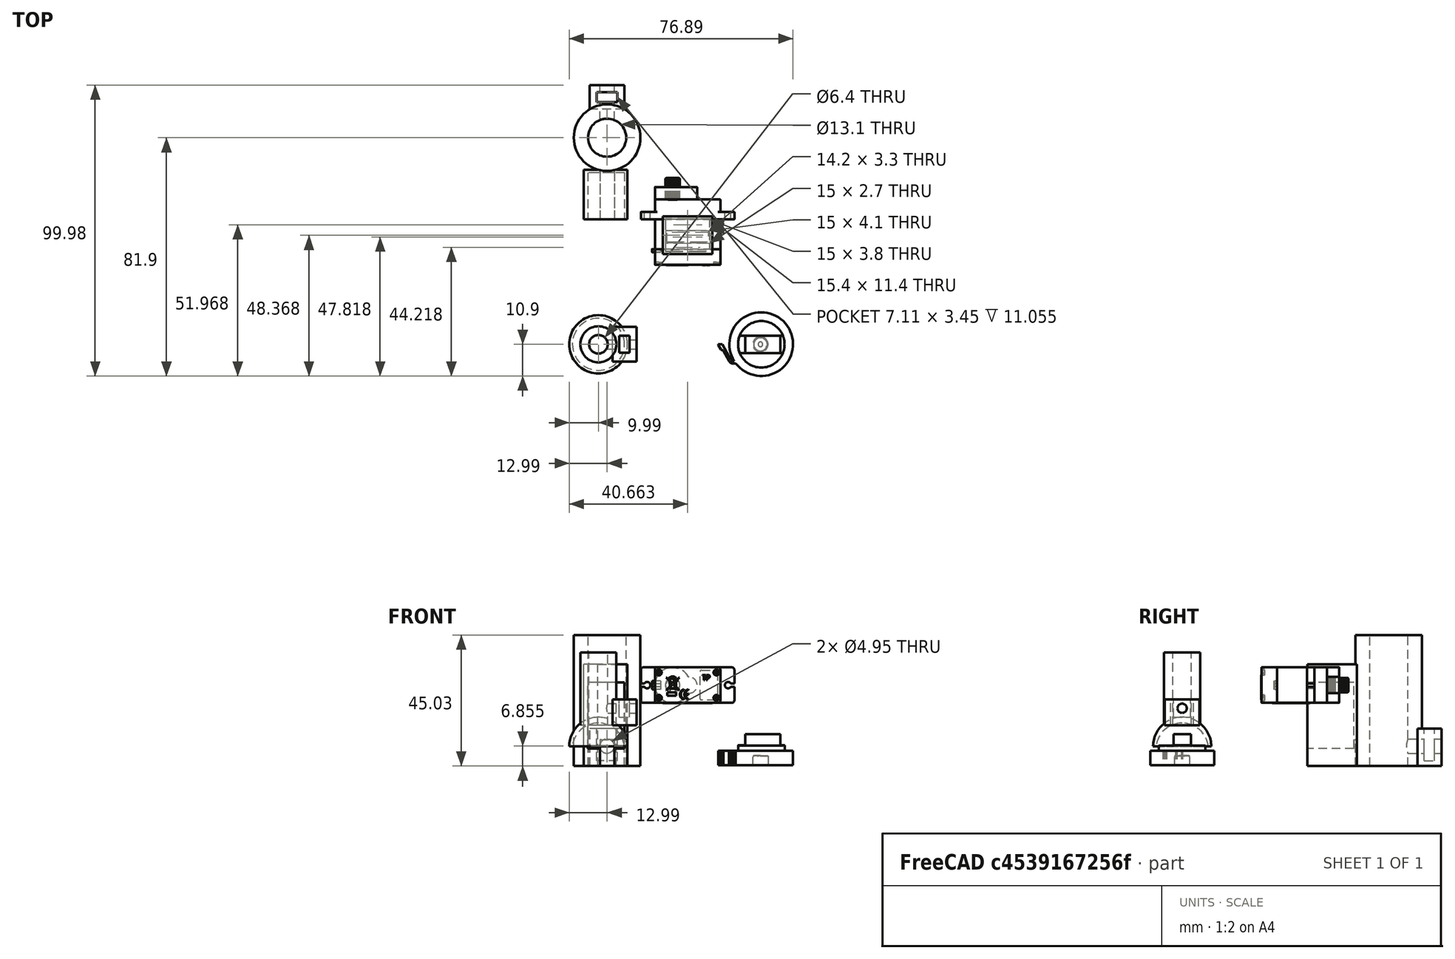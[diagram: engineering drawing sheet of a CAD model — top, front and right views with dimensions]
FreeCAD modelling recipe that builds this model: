
FCSTD DOCUMENT  (FreeCAD 0.19R24366 (Git))
Label: motor_fit_servo
License: All rights reserved
LicenseURL: http://en.wikipedia.org/wiki/All_rights_reserved
objects: Part::Feature×15, Part::Box×11, Part::Cut×9, Part::Cylinder×7, Part::Fuse×4, Part::MultiFuse×4, Sketcher::SketchObject×3, Mesh::Feature×2, Part::Extrusion×2, Part::Sphere×2, Part::Compound×2, Part::Compound2×1
note: 59 computed .brp shape members not serialized (recipe doc carries the construction recipe); baked Part::Feature solids carry a one-line shape summary decoded from their .brp

FEATURE [Part::Cylinder] cylinder
  Angle = 360
  AttacherType = Attacher::AttachEngine3D
  Height = 45
  Radius = 11.45
FEATURE [Part::Box] cube
  AttacherType = Attacher::AttachEngine3D
  Height = 12.91
  Length = 8.25
  Placement = pos=(-4.125,-5.955,-6.455) rot=(0,0,1;0rad)
  Width = 11.91
FEATURE [Part::Box] cube001
  AttacherType = Attacher::AttachEngine3D
  Height = 11.11
  Length = 3.45
  Placement = pos=(-1.725,-3.555,-4.6) rot=(0,0,1;0rad)
  Width = 7.11
FEATURE [Part::Cut] difference
  Base = -> cube
  Placement = pos=(13.95,0,6.425) rot=(0,0,1;0rad)
  Tool = -> cube001
FEATURE [Part::Fuse] union
  Base = -> cylinder
  Tool = -> difference
FEATURE [Part::Cylinder] cylinder001
  Angle = 360
  AttacherType = Attacher::AttachEngine3D
  Height = 50
  Placement = pos=(0,0,-1) rot=(0,0,1;0rad)
  Radius = 6.55
FEATURE [Part::Cylinder] cylinder002
  Angle = 360
  AttacherType = Attacher::AttachEngine3D
  Height = 22.9
  Placement = pos=(0,0,6.825) rot=(0,1,0;1.5708rad)
  Radius = 2.475
FEATURE [Part::Fuse] union001
  Base = -> cylinder001
  Tool = -> cylinder002
FEATURE [Part::Cut] difference001  label="poleFit"
  Base = -> union
  Tool = -> union001
FEATURE [Part::Box] Box  label="Cube"
  AttacherType = Attacher::AttachEngine3D
  Height = 17
  Length = 22.7
  Placement = pos=(0,0,1) rot=(0,0,1;0rad)
  Width = 12.6
FEATURE [Part::Box] Box001  label="Cube001"
  AttacherType = Attacher::AttachEngine3D
  Height = 17
  Length = 35
  Placement = pos=(-6,-1,0) rot=(0,0,1;0rad)
  Width = 15
FEATURE [Part::Cut] Cut
  Base = -> Box001
  Placement = pos=(-11,-6,6) rot=(0,-1,0;1.5708rad)
  Tool = -> Box
FEATURE [Part::Box] Box002  label="Cube002"
  AttacherType = Attacher::AttachEngine3D
  Height = 10
  Length = 20
  Placement = pos=(-30,-2.5,-1) rot=(0,0,1;0rad)
  Width = 5
FEATURE [Part::Cut] Cut001
  Base = -> Cut
  Tool = -> Box002
FEATURE [Part::MultiFuse] Fusion  label="motor_holder"
  Placement = pos=(-21,50,0) rot=(0,0,1;1.5708rad)
  Shapes = -> [difference001,Cut001]
FEATURE [Part::Feature] Solid
  shape: bbox 22.5 x 10.3 x 12.2 mm, 10 faces (baked)
FEATURE [Part::Feature] Solid001
  shape: bbox 17 x 13 x 0.1 mm, 50 faces (baked)
FEATURE [Part::Feature] Solid002
  shape: bbox 17 x 13 x 0.1 mm, 50 faces (baked)
FEATURE [Part::Feature] Solid003 .. Solid006  x4 (patterned run collapsed; names and placements below)
  shape: bbox 1.933 x 1 x 1.949 mm, 19 faces (baked)
FEATURE [Part::Feature] Solid007
  shape: bbox 22.64 x 5.5 x 12.34 mm, 157 faces (baked)
FEATURE [Part::Feature] Solid008
  shape: bbox 3 x 1 x 1 mm, 4 faces (baked)
FEATURE [Part::Feature] Solid009
  shape: bbox 3 x 1 x 1 mm, 4 faces (baked)
FEATURE [Part::Feature] Solid010
  shape: bbox 3 x 1 x 1 mm, 4 faces (baked)
FEATURE [Part::Feature] Solid011
  shape: bbox 32.1 x 11.05 x 13.21 mm, 102 faces (baked)
FEATURE [Part::Feature] Solid012
  shape: bbox 4.9 x 7.35 x 4.9 mm, 186 faces (baked)
FEATURE [Part::Compound2] Compound  label="SG90 Servo"
  Links = -> [Solid,Solid001,Solid002,Solid003,Solid004,Solid005,Solid006,Solid007,Solid008,Solid009,Solid010,Solid011,Solid012]
  Placement = pos=(-14.6069,45.1539,-46.0545) rot=(1,0,0;1.5708rad)
FEATURE [Mesh::Feature] Base
  Placement = pos=(0,0,0) rot=(1,0,0;1.5708rad)
FEATURE [Mesh::Feature] Freewheel_0_8mm  label="Freewheel_0.8mm"
  Placement = pos=(-63.4529,-2.9298,-37.056) rot=(0,0,1;0rad)
FEATURE [Sketcher::SketchObject] Sketch
  FullyConstrained = true
  Placement = pos=(0,0,0) rot=(0.57735,0.57735,0.57735;2.0944rad)
  sketch-geometry (37):
    g0: LineSegment StartX=76.2334 StartY=-16.1683 StartZ=0 EndX=76.2157 EndY=-16.287 EndZ=0
    g1: LineSegment StartX=76.2157 StartY=-16.287 StartZ=0 EndX=76.2042 EndY=-16.4372 EndZ=0
    g2: LineSegment StartX=76.2042 StartY=-16.4372 StartZ=0 EndX=76.2156 EndY=-16.5892 EndZ=0
    g3: LineSegment StartX=76.2156 StartY=-16.5892 StartZ=0 EndX=76.2528 EndY=-16.7393 EndZ=0
    g4: LineSegment StartX=76.2528 StartY=-16.7393 StartZ=0 EndX=76.312 EndY=-16.8829 EndZ=0
    g5: LineSegment StartX=76.312 StartY=-16.8829 StartZ=0 EndX=76.389 EndY=-17.0118 EndZ=0
    g6: LineSegment StartX=76.389 StartY=-17.0118 StartZ=0 EndX=76.4857 EndY=-17.1291 EndZ=0
    g7: LineSegment StartX=76.4857 StartY=-17.1291 StartZ=0 EndX=76.5997 EndY=-17.2306 EndZ=0
    g8: LineSegment StartX=76.5997 StartY=-17.2306 StartZ=0 EndX=76.7284 EndY=-17.3138 EndZ=0
    g9: LineSegment StartX=76.7284 StartY=-17.3138 StartZ=0 EndX=82.1149 EndY=-20.2387 EndZ=0
    g10: LineSegment StartX=82.1149 StartY=-20.2387 StartZ=0 EndX=82.1149 EndY=-21.7329 EndZ=0
    g11: LineSegment StartX=82.1149 StartY=-21.7329 StartZ=0 EndX=81.7891 EndY=-21.7293 EndZ=0
    g12: LineSegment StartX=81.7891 StartY=-21.7293 StartZ=0 EndX=80.304 EndY=-20.8014 EndZ=0
    g13: LineSegment StartX=80.304 StartY=-20.8014 StartZ=0 EndX=80.2423 EndY=-20.7557 EndZ=0
    g14: LineSegment StartX=80.2423 StartY=-20.7557 StartZ=0 EndX=80.188 EndY=-20.7011 EndZ=0
    g15: LineSegment StartX=80.188 StartY=-20.7011 StartZ=0 EndX=80.1429 EndY=-20.6389 EndZ=0
    g16: LineSegment StartX=80.1429 StartY=-20.6389 StartZ=0 EndX=80.1078 EndY=-20.5705 EndZ=0
    g17: LineSegment StartX=80.1078 StartY=-20.5705 StartZ=0 EndX=80.0837 EndY=-20.4975 EndZ=0
    g18: LineSegment StartX=80.0837 StartY=-20.4975 StartZ=0 EndX=80.071 EndY=-20.4217 EndZ=0
    g19: LineSegment StartX=80.071 StartY=-20.4217 StartZ=0 EndX=80.059 EndY=-20.2869 EndZ=0
    g20: LineSegment StartX=80.059 StartY=-20.2869 StartZ=0 EndX=80.0452 EndY=-20.2062 EndZ=0
    g21: LineSegment StartX=80.0452 StartY=-20.2062 StartZ=0 EndX=80.0182 EndY=-20.1286 EndZ=0
    g22: LineSegment StartX=80.0182 StartY=-20.1286 StartZ=0 EndX=79.9789 EndY=-20.0566 EndZ=0
    g23: LineSegment StartX=79.9789 StartY=-20.0566 StartZ=0 EndX=79.9285 EndY=-19.992 EndZ=0
    g24: LineSegment StartX=79.9285 StartY=-19.992 StartZ=0 EndX=79.8682 EndY=-19.9366 EndZ=0
    g25: LineSegment StartX=79.8682 StartY=-19.9366 StartZ=0 EndX=79.7996 EndY=-19.8917 EndZ=0
    g26: LineSegment StartX=79.7996 StartY=-19.8917 StartZ=0 EndX=76.3456 EndY=-18.0159 EndZ=0
    g27: LineSegment StartX=76.3456 StartY=-18.0159 StartZ=0 EndX=76.1153 EndY=-17.8672 EndZ=0
    g28: LineSegment StartX=76.1153 StartY=-17.8672 StartZ=0 EndX=75.9105 EndY=-17.6845 EndZ=0
    g29: LineSegment StartX=75.9105 StartY=-17.6845 StartZ=0 EndX=75.7345 EndY=-17.4732 EndZ=0
    g30: LineSegment StartX=75.7345 StartY=-17.4732 StartZ=0 EndX=75.5946 EndY=-17.2371 EndZ=0
    g31: LineSegment StartX=75.5946 StartY=-17.2371 StartZ=0 EndX=75.4903 EndY=-16.9821 EndZ=0
    g32: LineSegment StartX=75.4903 StartY=-16.9821 StartZ=0 EndX=75.4278 EndY=-16.7148 EndZ=0
    g33: LineSegment StartX=75.4278 StartY=-16.7148 StartZ=0 EndX=75.405 EndY=-16.4411 EndZ=0
    g34: LineSegment StartX=75.405 StartY=-16.4411 StartZ=0 EndX=75.4252 EndY=-16.1672 EndZ=0
    g35: LineSegment StartX=75.4252 StartY=-16.1672 StartZ=0 EndX=75.5014 EndY=-15.659 EndZ=0
    g36: ArcOfCircle CenterX=82.1156 CenterY=-6.93239 CenterZ=0 NormalX=0 NormalY=0 NormalZ=1 AngleXU=0 Radius=10.95 StartAngle=4.14528 EndAngle=10.347
  constraints (68):
    c: Coincident(g0,g1)
    c: Coincident(g1,g2)
    c: Coincident(g2,g3)
    c: Coincident(g3,g4)
    c: Coincident(g4,g5)
    c: Coincident(g5,g6)
    c: Coincident(g6,g7)
    c: Coincident(g7,g8)
    c: Coincident(g8,g9)
    c: Coincident(g9,g10)
    c: Vertical(g10)
    c: Coincident(g10,g11)
    c: Coincident(g11,g12)
    c: Coincident(g12,g13)
    c: Coincident(g13,g14)
    c: Coincident(g14,g15)
    c: Coincident(g15,g16)
    c: Coincident(g16,g17)
    c: Coincident(g17,g18)
    c: Coincident(g18,g19)
    c: Coincident(g19,g20)
    c: Coincident(g20,g21)
    c: Coincident(g21,g22)
    c: Coincident(g22,g23)
    c: Coincident(g23,g24)
    c: Coincident(g24,g25)
    c: Coincident(g25,g26)
    c: Coincident(g26,g27)
    c: Coincident(g27,g28)
    c: Coincident(g28,g29)
    c: Coincident(g29,g30)
    c: Coincident(g30,g31)
    c: Coincident(g31,g32)
    c: Coincident(g32,g33)
    c: Coincident(g33,g34)
    c: Coincident(g34,g35)
    c: Coincident(g36,g35)
    c: Coincident(g36,g0)
    c: Radius(g36) = 10.95
    c: Block(g35)
    c: Block(g1)
    c: Block(g0)
    c: Block(g2)
    c: Block(g3)
    c: Block(g4)
    c: Block(g5)
    c: Block(g6)
    c: Block(g34)
    c: Block(g33)
    c: Block(g32)
    c: Block(g31)
    c: Block(g30)
    c: Block(g29)
    c: Block(g28)
    c: Block(g27)
    c: Block(g7)
    c: Block(g8)
    c: Block(g9)
    c: Block(g26)
    c: Block(g11)
    c: Block(g12)
    c: Block(g14)
    c: Block(g17)
    c: Block(g20)
    c: Block(g22)
    c: Block(g24)
    c: Block(g19)
    c: Block(g16)
FEATURE [Part::Extrusion] Extrude
  Base = -> Sketch
  Dir = (1,0,0)
  DirMode = 2
  FaceMakerClass = Part::FaceMakerBullseye
  LengthFwd = 5
  LengthRev = 0
  Placement = pos=(6.88649,-82.0619,0.254467) rot=(0,1,0;1.5708rad)
  Solid = true
  Symmetric = false
FEATURE [Part::Cylinder] Cylinder006
  Angle = 360
  AttacherType = Attacher::AttachEngine3D
  Height = 6
  Radius = 8
FEATURE [Part::Box] Box003  label="Cube003"
  AttacherType = Attacher::AttachEngine3D
  Height = 25
  Length = 17
  Placement = pos=(-8.5,3,2) rot=(0,0,1;0rad)
  Width = 16
FEATURE [Part::Box] Box004  label="Cube004"
  AttacherType = Attacher::AttachEngine3D
  Height = 25
  Length = 17
  Placement = pos=(-8.5,-19,2) rot=(0,0,1;0rad)
  Width = 16
FEATURE [Part::Box] Box005  label="Cube005"
  AttacherType = Attacher::AttachEngine3D
  Height = 25
  Length = 17
  Placement = pos=(6.5,-3,2.1) rot=(0,0,1;0rad)
  Width = 16
FEATURE [Part::Box] Box006  label="Cube006"
  AttacherType = Attacher::AttachEngine3D
  Height = 25
  Length = 17
  Placement = pos=(-22.5,-12,2.1) rot=(0,0,1;0rad)
  Width = 16
FEATURE [Part::MultiFuse] Fusion001
  Shapes = -> [Box003,Box004,Box005,Box006]
FEATURE [Part::Cut] Cut004
  Base = -> Cylinder006
  Tool = -> Fusion001
FEATURE [Part::MultiFuse] Fusion002
  Shapes = -> [Cut004,Extrude]
FEATURE [Part::Feature] Solid026  label="servo_axis"
  Placement = pos=(0,27,0) rot=(1,0,0;1.5708rad)
  shape: bbox 4.9 x 4.9 x 7.35 mm, 186 faces (baked)
FEATURE [Sketcher::SketchObject] Sketch001
  FullyConstrained = true
  MapMode = 3
  Placement = pos=(0,27,0) rot=(1,0,0;3.14159rad)
  Support = -> [Solid026]
  sketch-geometry (1):
    g0: Circle CenterX=1.5221 CenterY=27.7817 CenterZ=0 NormalX=0 NormalY=0 NormalZ=1 AngleXU=0 Radius=2.6
  constraints (3):
    c: Radius(g0) = 2.6
    c: DistanceX(g0) = 1.5221
    c: DistanceY(g0) = 27.7817
FEATURE [Part::Extrusion] Extrude001
  Base = -> Sketch001
  Dir = (0,-2e-16,-1)
  DirMode = 2
  FaceMakerClass = Part::FaceMakerBullseye
  LengthFwd = 5
  LengthRev = 0
  Placement = pos=(0,0,36) rot=(0,0,1;0rad)
  Solid = true
  Symmetric = false
FEATURE [Part::MultiFuse] Fusion003
  Placement = pos=(-1.82363,0.770655,-37.5) rot=(0,0,1;0rad)
  Shapes = -> [Solid026,Extrude001]
FEATURE [Part::Cut] Cut005  label="motor_attachment"
  Base = -> Fusion002
  Placement = pos=(32,-21,5) rot=(0,0,1;0rad)
  Tool = -> Fusion003
FEATURE [Part::Box] cube002
  AttacherType = Attacher::AttachEngine3D
  Height = 8.91
  Length = 8.25
  Placement = pos=(-4.125,-5.955,-6.455) rot=(0,0,1;0rad)
  Width = 11.91
FEATURE [Part::Cylinder] cylinder003
  Angle = 360
  AttacherType = Attacher::AttachEngine3D
  Height = 50
  Placement = pos=(0,0,-1) rot=(0,0,1;0rad)
  Radius = 3.2
FEATURE [Part::Cylinder] cylinder004
  Angle = 360
  AttacherType = Attacher::AttachEngine3D
  Height = 25
  Radius = 6.2
FEATURE [Part::Box] cube003
  AttacherType = Attacher::AttachEngine3D
  Height = 11.11
  Length = 3.45
  Placement = pos=(-1.725,-2.9,-3.6) rot=(0,0,1;0rad)
  Width = 5.8
FEATURE [Part::Cylinder] cylinder005
  Angle = 360
  AttacherType = Attacher::AttachEngine3D
  Height = 22.9
  Placement = pos=(0,0,5.83) rot=(0,1,0;1.5708rad)
  Radius = 1.6
FEATURE [Part::Cut] difference002
  Base = -> cube002
  Placement = pos=(8.95,0,6.425) rot=(0,0,1;0rad)
  Tool = -> cube003
FEATURE [Part::Fuse] union002
  Base = -> cylinder003
  Tool = -> cylinder005
FEATURE [Part::Fuse] union003
  Base = -> cylinder004
  Tool = -> difference002
FEATURE [Part::Cut] difference003  label="wheel_fit_holder"
  Base = -> union003
  Tool = -> union002
FEATURE [Part::Sphere] Sphere
  Angle1 = -90
  Angle2 = 0
  Angle3 = 360
  AttacherType = Attacher::AttachEngine3D
  Placement = pos=(16.5428,-16.9323,-1e-16) rot=(0,0,1;0rad)
  Radius = 10
FEATURE [Part::Sphere] Sphere001
  Angle1 = -90
  Angle2 = 0
  Angle3 = 360
  AttacherType = Attacher::AttachEngine3D
  Placement = pos=(16.5428,-16.9323,1) rot=(0,0,1;0rad)
  Radius = 9
FEATURE [Part::Cut] Cut006
  Base = -> Sphere
  Placement = pos=(-0.04745,0.430952,1) rot=(0,0,1;0rad)
  Tool = -> Sphere001
FEATURE [Sketcher::SketchObject] Sketch002
  FullyConstrained = true
  MapMode = 3
  Placement = pos=(0,0,0) rot=(1,0,0;3.14159rad)
  Support = -> [Base]
  sketch-geometry (1):
    g0: Circle CenterX=16.4953 CenterY=16.5013 CenterZ=0 NormalX=0 NormalY=0 NormalZ=1 AngleXU=0 Radius=8
  constraints (2):
    c: Radius(g0) = 8
    c: Block(g0)
FEATURE [Part::Feature] Base002
  shape: bbox 32.96 x 33 x 8 mm, 664 faces, 0 solids (baked)
FEATURE [Part::Compound] Compound001
  Links = -> [Cut006,Base002]
  Placement = pos=(-16.49,-16.5,-6.25) rot=(1,0,0;3.14159rad)
FEATURE [Part::Compound] Compound002  label="wheel_assembly"
  Links = -> [difference003,Compound001]
  Placement = pos=(-24,-21,14) rot=(0,0,1;0rad)
